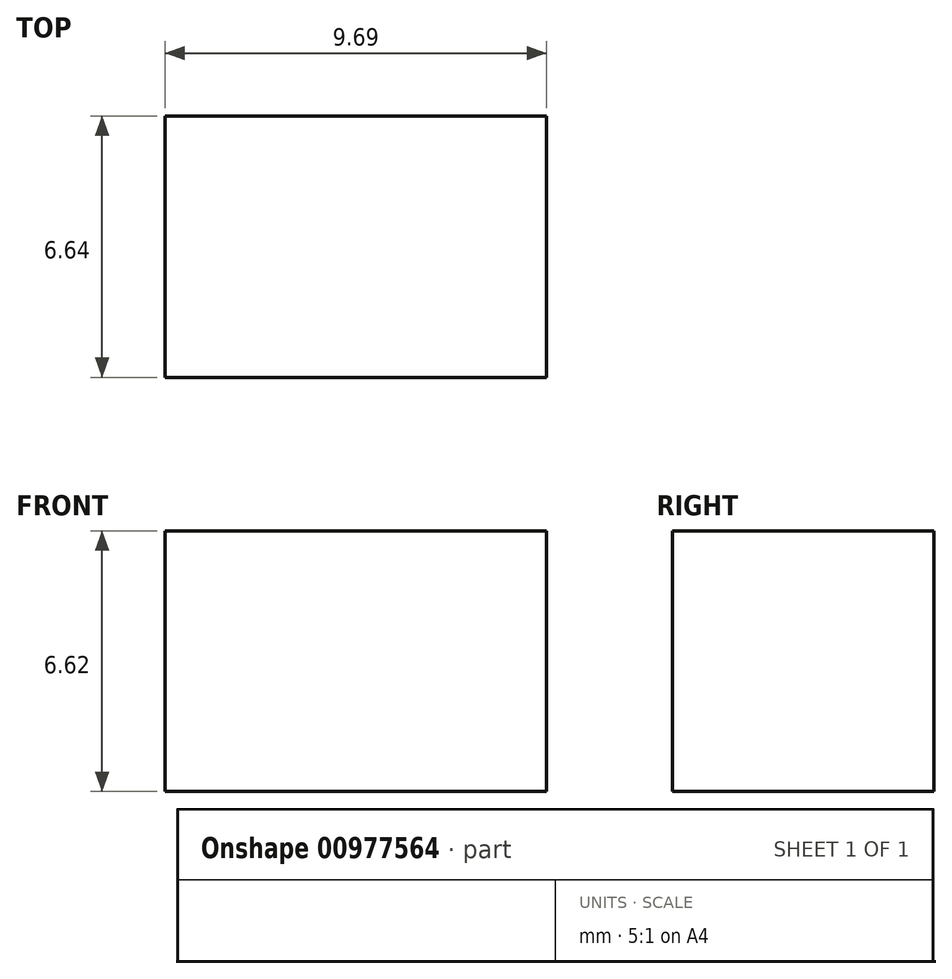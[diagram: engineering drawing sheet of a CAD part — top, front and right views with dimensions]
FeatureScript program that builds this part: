
annotation { "Feature Type Name" : "Feature", "Feature Type Description" : "" }
export const myFeature = defineFeature(function(context is Context, id is Id, definition is map)
    precondition{}
    {
        {
            var Q0;
            Q0=qCreatedBy(makeId("Top.planeOp"),FACE);
            var sketch = newSketch(context, id + "F0", { "sketchPlane" : qUnion([Q0])});
            skLineSegment(sketch, "E0.bottom", {"start": v(-32.99, 29.18) * mm, "end": v(-23.3, 29.18) * mm});
            skLineSegment(sketch, "E0.top", {"start": v(-32.99, 22.54) * mm, "end": v(-23.3, 22.54) * mm});
            skLineSegment(sketch, "E0.left", {"start": v(-32.99, 29.18) * mm, "end": v(-32.99, 22.54) * mm});
            skLineSegment(sketch, "E0.right", {"start": v(-23.3, 29.18) * mm, "end": v(-23.3, 22.54) * mm});
            skSolve(sketch);
        }
        {
            var Q0;
            Q0 = qSketchRegion(id + "F0", true);
            extrude(context, id + "F1", {"entities" : qUnion([Q0]), "depth" : 6.62 * mm, "offsetDistance" : 25.4 * mm});
        }
    });
